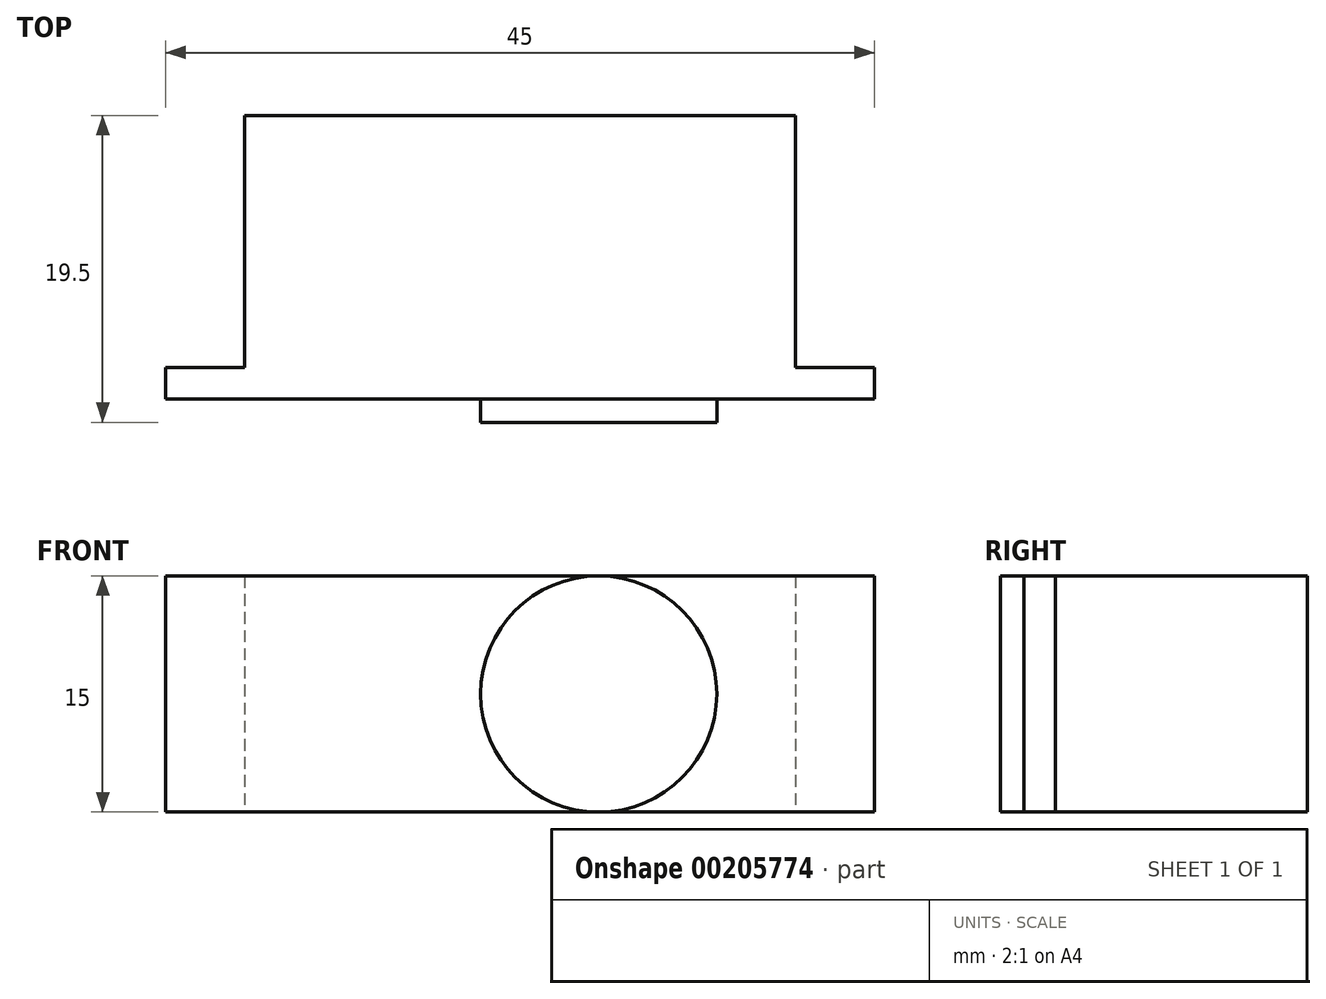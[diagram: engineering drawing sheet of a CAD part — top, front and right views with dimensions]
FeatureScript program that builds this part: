
annotation { "Feature Type Name" : "Feature", "Feature Type Description" : "" }
export const myFeature = defineFeature(function(context is Context, id is Id, definition is map)
    precondition{}
    {
        {
            var Q0;
            Q0=qCreatedBy(makeId("Top.planeOp"),FACE);
            var sketch = newSketch(context, id + "F0", { "sketchPlane" : qUnion([Q0])});
            skLineSegment(sketch, "E0", {"start": v(0, 0) * mm, "end": v(0, 4.5) * mm, "construction": true});
            skLineSegment(sketch, "E1", {"start": v(0, 4.5) * mm, "end": v(17.5, 4.5) * mm});
            skLineSegment(sketch, "E2", {"start": v(17.5, 4.5) * mm, "end": v(17.5, 6.5) * mm});
            skLineSegment(sketch, "E3", {"start": v(17.5, 6.5) * mm, "end": v(12.5, 6.5) * mm});
            skLineSegment(sketch, "E4", {"start": v(12.5, 6.5) * mm, "end": v(12.5, 22.5) * mm});
            skLineSegment(sketch, "E5", {"start": v(12.5, 22.5) * mm, "end": v(-22.5, 22.5) * mm});
            skLineSegment(sketch, "E6", {"start": v(-22.5, 22.5) * mm, "end": v(-22.5, 6.5) * mm});
            skLineSegment(sketch, "E7", {"start": v(-22.5, 6.5) * mm, "end": v(-27.5, 6.5) * mm});
            skLineSegment(sketch, "E8", {"start": v(-27.5, 6.5) * mm, "end": v(-27.5, 4.5) * mm});
            skLineSegment(sketch, "E9", {"start": v(-27.5, 4.5) * mm, "end": v(0, 4.5) * mm});
            skLineSegment(sketch, "E10", {"start": v(7.5, 4.5) * mm, "end": v(7.5, 3) * mm});
            skLineSegment(sketch, "E11", {"start": v(7.5, 3) * mm, "end": v(0, 3) * mm});
            skLineSegment(sketch, "E12", {"start": v(0, 3) * mm, "end": v(-7.5, 3) * mm});
            skLineSegment(sketch, "E13", {"start": v(-7.5, 3) * mm, "end": v(-7.5, 4.5) * mm});
            skLineSegment(sketch, "E14", {"start": v(-22.5, 6.5) * mm, "end": v(12.5, 6.5) * mm, "construction": true});
            skPoint(sketch, "E15.orphan", {"position": v(0, 22.5) * mm});
            skLineSegment(sketch, "E16", {"start": v(0, 4.5) * mm, "end": v(0, 3) * mm});
            skSolve(sketch);
        }
        {
            var Q0;
            {var subQ6=sQuery(id+"F0.wireOp",EDGE,"E2");Q0=makeQuery(id+"F0.imprint","IMPRINT",FACE,{"disambiguationData":[TD([[makeQuery(id+"F0.imprint","IMPRINT",EDGE,{"derivedFrom":subQ6}),1.0]])]});}
            extrude(context, id + "F1", {"entities" : qUnion([Q0]), "depth" : 15 * mm, "symmetric" : true});
        }
        {
            var Q0;
            {var subQ2=sQuery(id+"F0.wireOp",EDGE,"E10");Q0=makeQuery(id+"F0.imprint","IMPRINT",FACE,{"disambiguationData":[TD([[makeQuery(id+"F0.imprint","IMPRINT",EDGE,{"derivedFrom":subQ2}),-1.0]])]});}
            var Q1;
            Q1=sQuery(id+"F0.wireOp",EDGE,"E0");
            revolve(context, id + "F2", {"operationType" : NewBodyOperationType.ADD, "entities" : qUnion([Q0]), "axis" : qUnion([Q1]), "revolveType" : RevolveType.FULL});
        }
    });
